# Revit family: HL_Сифон для писсуаров_HL130
name_source: partatom
category: Příslušenství trubek
revit_build: Autodesk Revit 2016 (Build: 20161004_0715(x64)
units: mm (PartAtom-declared; Revit-internal decimal feet)

## family parameters
Kóta kulaté spojky = Použít průměr
Nadpis OmniClass = General Pipework and Ductwork Products
Ořezat dutým tvarem při načtení = Ne
Sdílené = Ne
Typ součásti = Normální
Vždy vertikální = Ano
Založené na pracovní rovině = Ne
Číslo OmniClass = 23.60.30.00

## types (2) — shared parameters
URL = http://www.hutterer-lechner.com
Výrobce = HL Hutterer & Lechner GmbH
МАТЕРИАЛ = PP
НОМИНАЛЬНЫЙ ДИАМЕТР = 50 mm
ПРОИЗВОДИТЕЛЬНОСТЬ = 0,7l/s
ПРОПУСКНАЯ СПОСОБНОСТЬ = 0.0 m³/h
материал = Plactic - White
zero-valued in all types: Cena

## per-type parameters (varying)
| type | EAN | Klíčová poznámka | Komentáře k typům | Model | Popis | b | c | ВЕС | НОМИНАЛЬНЫЙ ДИАМЕТР 2 | РАЗМЕР |
| HL130_40 | 9003076013043 | HL130/40 | Сифон для писсуаров DN40 с соединительной манжетой и декоративной розеткой. | HL130/40 | Сифон для писсуаров DN40 | 193 mm | 20 mm  [stored 0.0656168 ft] | 0,265 kg | 40 mm | DN40 |
| HL130_30 | 9003076301300 | HL130/30 | Сифон для писсуаров DN32 с соединительной манжетой и декоративной розеткой. | HL130/30 | Сифон для писсуаров DN32 | 189 mm | 16 mm  [stored 0.0524934 ft] | 0,267 kg | 32 mm | DN32 |

note: [stored X ft] marks values corroborated as IEEE doubles in the binary element streams (Revit-internal decimal feet)
